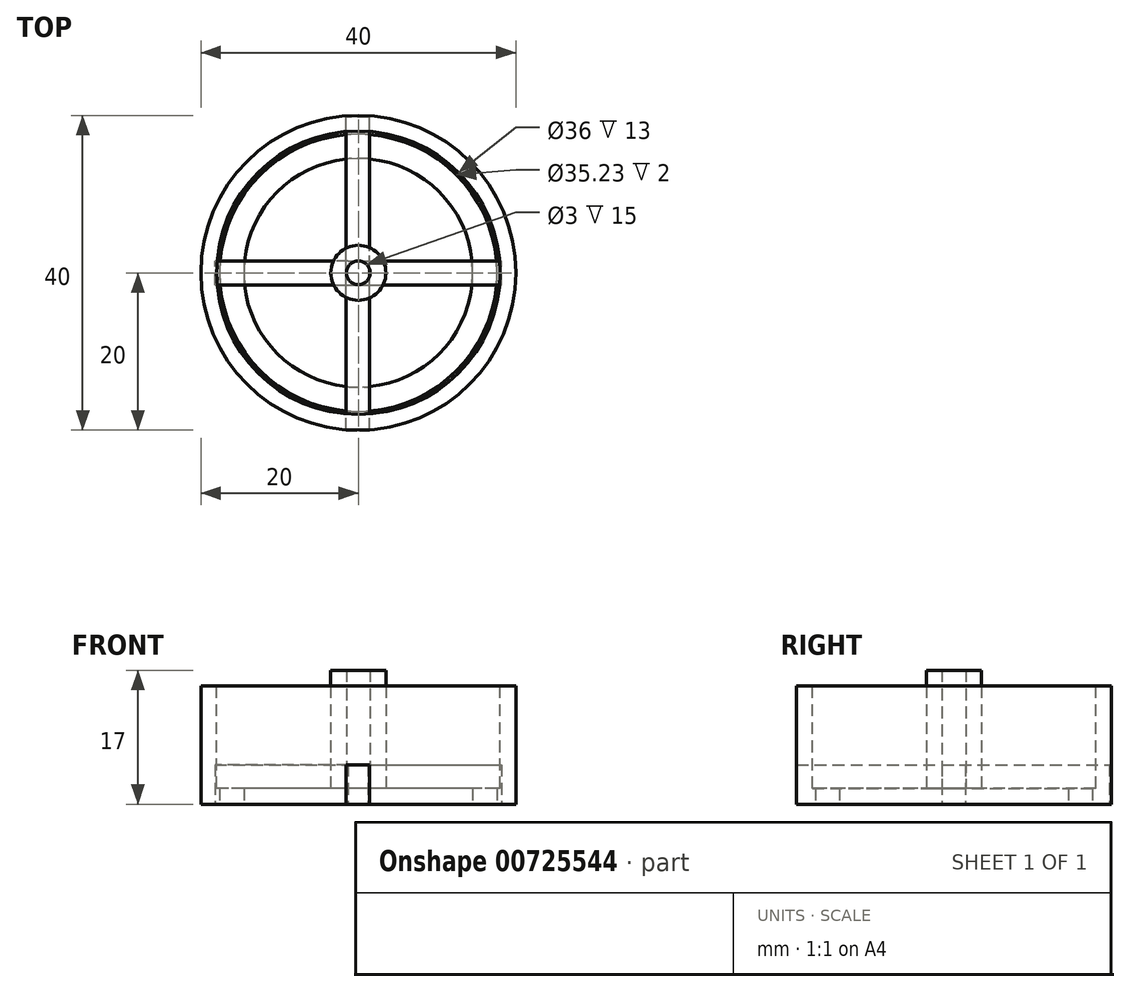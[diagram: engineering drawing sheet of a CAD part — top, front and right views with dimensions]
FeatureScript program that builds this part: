
annotation { "Feature Type Name" : "Feature", "Feature Type Description" : "" }
export const myFeature = defineFeature(function(context is Context, id is Id, definition is map)
    precondition{}
    {
        {
            var Q0;
            Q0=qCreatedBy(makeId("Top.planeOp"),FACE);
            var sketch = newSketch(context, id + "F0", { "sketchPlane" : qUnion([Q0])});
            skCircle(sketch, "E0", {"center": v(0, 0) * mm, "radius": 20 * mm});
            skSolve(sketch);
        }
        {
            var Q0;
            Q0=makeQuery(id+"F0.imprint","IMPRINT",FACE,{"disambiguationData":[TD([[makeQuery(id+"F0.imprint","IMPRINT",EDGE,{"derivedFrom":sQuery(id+"F0.wireOp",EDGE,"E0")}),1.0]])]});
            extrude(context, id + "F1", {"entities" : qUnion([Q0]), "depth" : 15 * mm, "offsetDistance" : 25 * mm});
        }
        {
            var Q0;
            Q0=makeQuery(id+"F1.opExtrude","CAP_FACE",FACE,{"disambiguationData":[OSD([sQuery(id+"F0.wireOp",EDGE,"E0")])],"isStart":false});
            var sketch = newSketch(context, id + "F2", { "sketchPlane" : qUnion([Q0])});
            skCircle(sketch, "E1", {"center": v(0, 0) * mm, "radius": 18 * mm});
            skSolve(sketch);
        }
        {
            var Q0;
            Q0=makeQuery(id+"F2.imprint","IMPRINT",FACE,{"disambiguationData":[TD([[makeQuery(id+"F2.imprint","IMPRINT",EDGE,{"derivedFrom":sQuery(id+"F2.wireOp",EDGE,"E1")}),1.0]])]});
            extrude(context, id + "F3", {"entities" : qUnion([Q0]), "operationType" : NewBodyOperationType.REMOVE, "oppositeDirection" : true, "depth" : 13 * mm, "offsetDistance" : 25 * mm});
        }
        {
            var Q0;
            Q0=makeQuery(id+"F3.boolean.opBoolean","COPY",FACE,{"derivedFrom":makeQuery(id+"F3.opExtrude","CAP_FACE",FACE,{"disambiguationData":[OSD([sQuery(id+"F2.wireOp",EDGE,"E1")])],"isStart":false})});
            var sketch = newSketch(context, id + "F4", { "sketchPlane" : qUnion([Q0])});
            skCircle(sketch, "E2", {"center": v(0, 0) * mm, "radius": 1.5 * mm});
            skCircle(sketch, "E3", {"center": v(0, 0) * mm, "radius": 3.5 * mm});
            skSolve(sketch);
        }
        {
            var Q0;
            Q0=makeQuery(id+"F4.imprint","IMPRINT",FACE,{"disambiguationData":[TD([[makeQuery(id+"F4.imprint","IMPRINT",EDGE,{"derivedFrom":sQuery(id+"F4.wireOp",EDGE,"E2")}),-1.0]])]});
            extrude(context, id + "F5", {"entities" : qUnion([Q0]), "operationType" : NewBodyOperationType.ADD, "depth" : 15 * mm, "offsetDistance" : 25 * mm});
        }
        {
            var Q0;
            Q0=makeQuery(id+"F1.opExtrude","CAP_FACE",FACE,{"disambiguationData":[OSD([sQuery(id+"F0.wireOp",EDGE,"E0")])],"isStart":true});
            var sketch = newSketch(context, id + "F6", { "sketchPlane" : qUnion([Q0])});
            skPoint(sketch, "E4.center", {"position": v(0, 0) * mm});
            skPoint(sketch, "E5.endSnap0", {"position": v(6.33, -7.74) * mm});
            skCircle(sketch, "E6", {"center": v(0, 0) * mm, "radius": 14.54 * mm});
            skCircle(sketch, "E7", {"center": v(0, 0) * mm, "radius": 17.62 * mm});
            skSolve(sketch);
        }
        {
            var Q0;
            Q0=qSketchRegion(id+"F6",true);
            extrude(context, id + "F7", {"entities" : qUnion([Q0]), "operationType" : NewBodyOperationType.REMOVE, "oppositeDirection" : true, "depth" : 25 * mm, "offsetDistance" : 25 * mm});
        }
        {
            var Q0;
            Q0=makeQuery(id+"F6.imprint","IMPRINT",FACE,{"disambiguationData":[TD([[makeQuery(id+"F6.imprint","IMPRINT",EDGE,{"derivedFrom":sQuery(id+"F6.wireOp",EDGE,"E6")}),-1.0]])]});
            extrude(context, id + "F8", {"entities" : qUnion([Q0]), "operationType" : NewBodyOperationType.REMOVE, "oppositeDirection" : true, "depth" : 25 * mm, "offsetDistance" : 25 * mm});
        }
        {
            var Q0;
            Q0=qCreatedBy(makeId("Top.planeOp"),FACE);
            var sketch = newSketch(context, id + "F9", { "sketchPlane" : qUnion([Q0])});
            skLineSegment(sketch, "E8", {"start": v(-1.57, 0) * mm, "end": v(1.43, 0) * mm});
            skPoint(sketch, "E9.end.orphan", {"position": v(0, 19.97) * mm});
            skLineSegment(sketch, "E10", {"start": v(-1.57, 0) * mm, "end": v(-1.57, 19.8) * mm});
            skLineSegment(sketch, "E11", {"start": v(1.43, 0) * mm, "end": v(1.43, 19.74) * mm});
            skLineSegment(sketch, "E12", {"start": v(1.43, 19.74) * mm, "end": v(-1.57, 19.8) * mm});
            skLineSegment(sketch, "E13", {"start": v(-1.57, -20) * mm, "end": v(1.43, -20) * mm});
            skLineSegment(sketch, "E14", {"start": v(1.43, -20) * mm, "end": v(1.43, 0) * mm});
            skLineSegment(sketch, "E15", {"start": v(-1.57, -20) * mm, "end": v(-1.57, 0) * mm});
            skSolve(sketch);
        }
        {
            var Q0;
            Q0=qSketchRegion(id+"F9",true);
            extrude(context, id + "F10", {"entities" : qUnion([Q0]), "depth" : 5 * mm, "offsetDistance" : 25 * mm});
        }
        {
            var Q0;
            Q0=qCreatedBy(makeId("Top.planeOp"),FACE);
            var sketch = newSketch(context, id + "F11", { "sketchPlane" : qUnion([Q0])});
            skArc(sketch, "E16", {"start": v(-1.3, -1.47) * mm, "mid": v(-1.25, -1.5) * mm, "end": v(-1.22, -1.53) * mm});
            skLineSegment(sketch, "E17.bottom", {"start": v(-1.3, 1.47) * mm, "end": v(1.22, 1.47) * mm});
            skLineSegment(sketch, "E17.top", {"start": v(-1.3, -1.53) * mm, "end": v(1.22, -1.53) * mm});
            skLineSegment(sketch, "E17.left", {"start": v(-1.3, 1.47) * mm, "end": v(-1.3, 1.47) * mm});
            skLineSegment(sketch, "E17.right", {"start": v(1.22, 1.47) * mm, "end": v(1.22, 1.47) * mm});
            skLineSegment(sketch, "E18.bottom", {"start": v(1.22, -1.53) * mm, "end": v(18.22, -1.53) * mm});
            skLineSegment(sketch, "E18.top", {"start": v(1.22, 1.47) * mm, "end": v(18.22, 1.47) * mm});
            skLineSegment(sketch, "E18.right", {"start": v(18.22, -1.53) * mm, "end": v(18.22, 1.47) * mm});
            skLineSegment(sketch, "E19.bottom", {"start": v(-1.3, -1.53) * mm, "end": v(-18.22, -1.53) * mm});
            skLineSegment(sketch, "E19.top", {"start": v(-1.3, 1.47) * mm, "end": v(-18.22, 1.47) * mm});
            skLineSegment(sketch, "E19.left", {"start": v(-1.3, -1.53) * mm, "end": v(-1.3, -1.47) * mm});
            skLineSegment(sketch, "E19.right", {"start": v(-18.22, -1.53) * mm, "end": v(-18.22, 1.47) * mm});
            skLineSegment(sketch, "E20.trimOffspring", {"start": v(-1.3, -1.47) * mm, "end": v(-1.3, -1.53) * mm});
            skArc(sketch, "E21.trimOffspring", {"start": v(-1.3, 1.47) * mm, "mid": v(-1.3, 1.47) * mm, "end": v(-1.3, 1.47) * mm});
            skSolve(sketch);
        }
        {
            var Q0;
            Q0=qSketchRegion(id+"F11",true);
            extrude(context, id + "F12", {"entities" : qUnion([Q0]), "depth" : 5 * mm, "offsetDistance" : 25 * mm});
        }
    });
